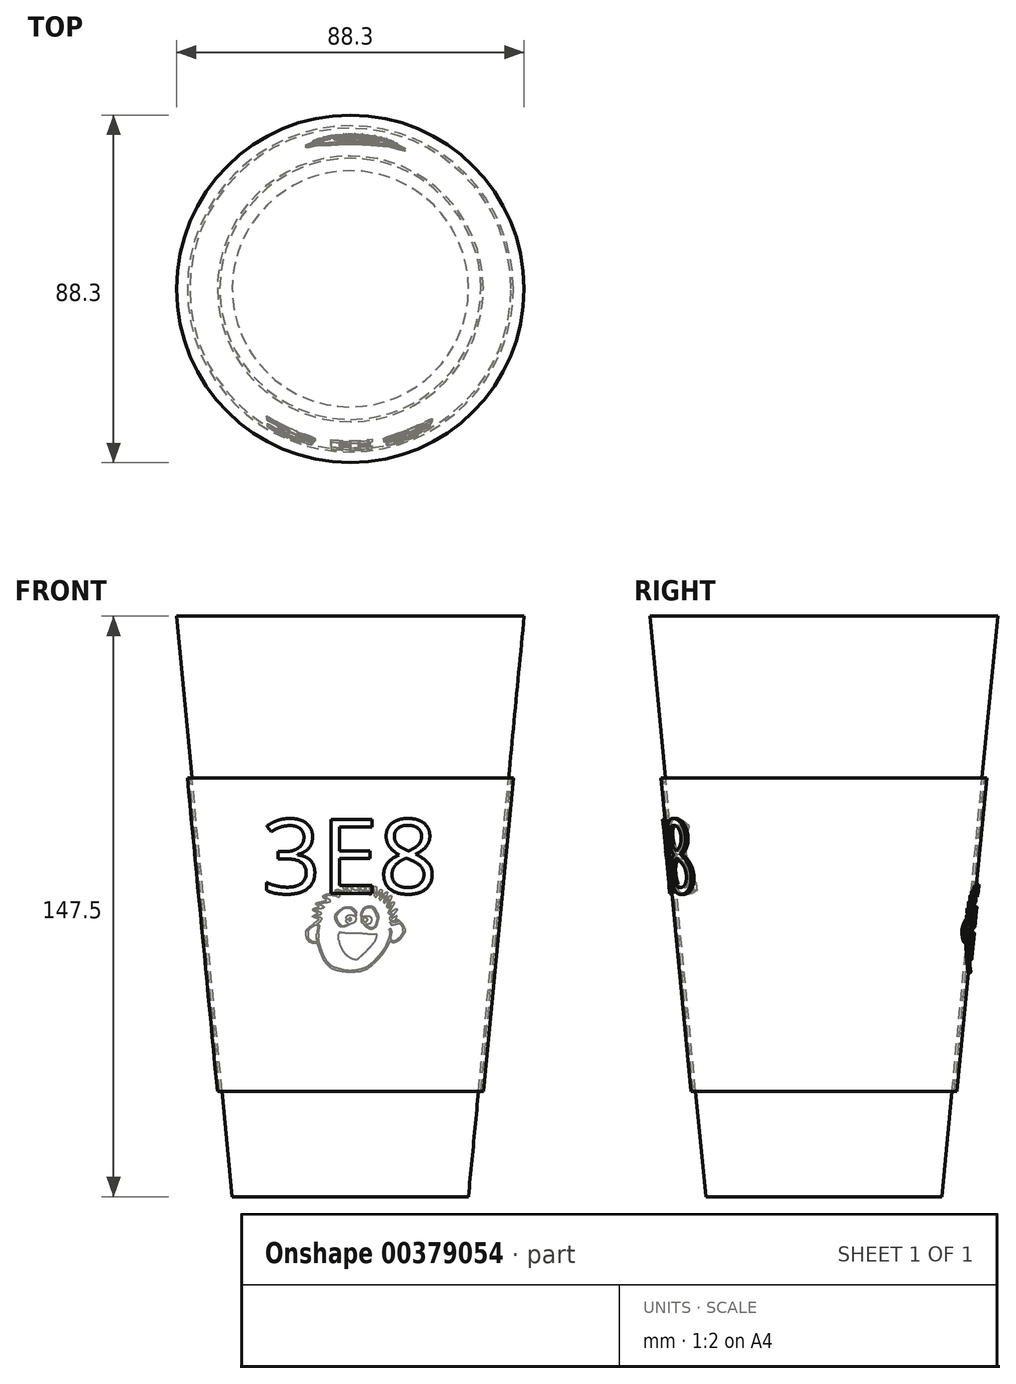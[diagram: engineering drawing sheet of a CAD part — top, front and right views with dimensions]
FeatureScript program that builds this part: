
annotation { "Feature Type Name" : "Feature", "Feature Type Description" : "" }
export const myFeature = defineFeature(function(context is Context, id is Id, definition is map)
    precondition{}
    {
        {
            var Q0;
            Q0=qCreatedBy(makeId("Top.planeOp"),FACE);
            var sketch = newSketch(context, id + "F0", { "sketchPlane" : qUnion([Q0])});
            skCircle(sketch, "E0", {"center": v(0, 0) * mm, "radius": 30 * mm});
            skSolve(sketch);
        }
        {
            var Q0;
            Q0=qCreatedBy(makeId("Top.planeOp"),FACE);
            cPlane(context, id + "F1", {"entities" : qUnion([Q0]), "cplaneType" : CPlaneType.OFFSET, "offset" : 147.5 * mm, "width" : 150 * mm, "height" : 150 * mm});
        }
        {
            var Q0;
            Q0=qCreatedBy(id+"F1.planeOp",FACE);
            var sketch = newSketch(context, id + "F2", { "sketchPlane" : qUnion([Q0])});
            skCircle(sketch, "E1", {"center": v(0, 0) * mm, "radius": 44.15 * mm});
            skSolve(sketch);
        }
        {
            var Q0;
            Q0=makeQuery(id+"F0.imprint","IMPRINT",FACE,{"disambiguationData":[TD([[makeQuery(id+"F0.imprint","IMPRINT",EDGE,{"derivedFrom":sQuery(id+"F0.wireOp",EDGE,"E0")}),1.0]])]});
            var Q1;
            Q1=makeQuery(id+"F2.imprint","IMPRINT",FACE,{"disambiguationData":[TD([[makeQuery(id+"F2.imprint","IMPRINT",EDGE,{"derivedFrom":sQuery(id+"F2.wireOp",EDGE,"E1")}),1.0]])]});
            loft(context, id + "F3", {"sheetProfilesArray" : [{ "sheetProfileEntities" : qUnion([Q0]) }, { "sheetProfileEntities" : qUnion([Q1]) }]});
        }
        {
            var Q0;
            Q0=qCreatedBy(makeId("Front.planeOp"),FACE);
            var sketch = newSketch(context, id + "F4", { "sketchPlane" : qUnion([Q0])});
            skLineSegment(sketch, "E2", {"start": v(44.15, 147.5) * mm, "end": v(30, 0) * mm, "construction": true});
            skLineSegment(sketch, "E3", {"start": v(-30, 0) * mm, "end": v(-44.15, 147.5) * mm, "construction": true});
            skLineSegment(sketch, "E4", {"start": v(0, 0) * mm, "end": v(0, 147.5) * mm, "construction": true});
            skLineSegment(sketch, "E5", {"start": v(-40.21, 106.44) * mm, "end": v(-40.81, 106.44) * mm, "construction": true});
            skLineSegment(sketch, "E6", {"start": v(-40.81, 106.44) * mm, "end": v(-33.18, 26.86) * mm});
            skLineSegment(sketch, "E7", {"start": v(-33.18, 26.86) * mm, "end": v(-33.77, 26.8) * mm});
            skLineSegment(sketch, "E8", {"start": v(-33.77, 26.8) * mm, "end": v(-41.41, 106.44) * mm});
            skLineSegment(sketch, "E9", {"start": v(-41.41, 106.44) * mm, "end": v(-40.81, 106.44) * mm});
            skLineSegment(sketch, "E10", {"start": v(-41.41, 106.44) * mm, "end": v(-42.01, 106.44) * mm, "construction": true});
            skLineSegment(sketch, "E11", {"start": v(-42.01, 106.44) * mm, "end": v(-62.01, 106.44) * mm});
            skLineSegment(sketch, "E12", {"start": v(-62.01, 106.44) * mm, "end": v(-54.37, 26.8) * mm});
            skLineSegment(sketch, "E13", {"start": v(-54.37, 26.8) * mm, "end": v(-34.55, 28.7) * mm});
            skLineSegment(sketch, "E14", {"start": v(-34.55, 28.7) * mm, "end": v(-42.01, 106.44) * mm});
            skSolve(sketch);
        }
        {
            var Q0;
            Q0=makeQuery(id+"F4.imprint","IMPRINT",FACE,{"disambiguationData":[TD([[makeQuery(id+"F4.imprint","IMPRINT",EDGE,{"derivedFrom":sQuery(id+"F4.wireOp",EDGE,"E6")}),-1.0]])]});
            var Q1;
            Q1=sQuery(id+"F4.wireOp",EDGE,"E4");
            revolve(context, id + "F5", {"entities" : qUnion([Q0]), "axis" : qUnion([Q1]), "revolveType" : RevolveType.FULL});
        }
        {
            var Q0;
            Q0=qCreatedBy(makeId("Front.planeOp"),FACE);
            cPlane(context, id + "F6", {"entities" : qUnion([Q0]), "cplaneType" : CPlaneType.OFFSET, "offset" : 45 * mm, "width" : 150 * mm, "height" : 150 * mm});
        }
        {
            var Q0;
            Q0=qCreatedBy(makeId("Front.planeOp"),FACE);
            cPlane(context, id + "F7", {"entities" : qUnion([Q0]), "cplaneType" : CPlaneType.OFFSET, "offset" : 50 * mm, "oppositeDirection" : true, "width" : 150 * mm, "height" : 150 * mm});
        }
        {
            var Q0;
            Q0=qCreatedBy(id+"F6.planeOp",FACE);
            var sketch = newSketch(context, id + "F8", { "sketchPlane" : qUnion([Q0])});
            skLineSegment(sketch, "E15.0", {"start": v(41.41, 106.44) * mm, "end": v(-41.41, 106.44) * mm, "construction": true});
            skLineSegment(sketch, "E16.0", {"start": v(33.77, 26.8) * mm, "end": v(-33.77, 26.8) * mm, "construction": true});
            skText(sketch, "E17", { "text": "3E8", "fontName": "OpenSans-Regular.ttf"});
            skLineSegment(sketch, "E18", {"start": v(0, 81.8) * mm, "end": v(0, 106.44) * mm, "construction": true});
            skLineSegment(sketch, "E19", {"start": v(0, 51.43) * mm, "end": v(0, 26.8) * mm, "construction": true});
            const initialGuessF8  = {"E17": [-0.0225, 0.07707, 1, 0, 0.01892]};
            skSetInitialGuess(sketch, initialGuessF8);
            skSolve(sketch);
        }
        {
            var Q0;
            Q0=qCreatedBy(id+"F7.planeOp",FACE);
            var sketch = newSketch(context, id + "F9", { "sketchPlane" : qUnion([Q0])});
            skPoint(sketch, "E20.0", {"position": v(0, 81.8) * mm});
            skLineSegment(sketch, "E21", {"start": v(-7.97, 70.42) * mm, "end": v(-9.11, 69.59) * mm});
            skLineSegment(sketch, "E22", {"start": v(-9.11, 69.59) * mm, "end": v(-9.2, 69.3) * mm});
            skLineSegment(sketch, "E23", {"start": v(-9.2, 69.3) * mm, "end": v(-10.22, 68.66) * mm});
            skLineSegment(sketch, "E24", {"start": v(-10.22, 68.66) * mm, "end": v(-10.84, 68.07) * mm});
            skLineSegment(sketch, "E25", {"start": v(-10.84, 68.07) * mm, "end": v(-11.27, 67.43) * mm});
            skLineSegment(sketch, "E26", {"start": v(-11.27, 67.43) * mm, "end": v(-11.27, 66.6) * mm});
            skLineSegment(sketch, "E27", {"start": v(-11.27, 66.6) * mm, "end": v(-10.97, 65.33) * mm});
            skLineSegment(sketch, "E28", {"start": v(-10.97, 65.33) * mm, "end": v(-10.29, 64.62) * mm});
            skLineSegment(sketch, "E29", {"start": v(-10.29, 64.62) * mm, "end": v(-9.45, 64.34) * mm});
            skLineSegment(sketch, "E30", {"start": v(-8.34, 64.34) * mm, "end": v(-7.57, 62) * mm});
            skLineSegment(sketch, "E31", {"start": v(-7.57, 62) * mm, "end": v(-6.64, 59.9) * mm});
            skLineSegment(sketch, "E32", {"start": v(-6.64, 59.9) * mm, "end": v(-5.4, 58.47) * mm});
            skLineSegment(sketch, "E33", {"start": v(-5.4, 58.47) * mm, "end": v(-4.48, 57.76) * mm});
            skLineSegment(sketch, "E34", {"start": v(-4.48, 57.76) * mm, "end": v(-3.1, 57.36) * mm});
            skLineSegment(sketch, "E35", {"start": v(-3.1, 57.36) * mm, "end": v(-1.77, 57.1) * mm});
            skLineSegment(sketch, "E36", {"start": v(-1.77, 57.1) * mm, "end": v(0.1, 56.93) * mm});
            skLineSegment(sketch, "E37", {"start": v(0.1, 56.93) * mm, "end": v(2.49, 57.16) * mm});
            skLineSegment(sketch, "E38", {"start": v(2.49, 57.16) * mm, "end": v(4.18, 57.73) * mm});
            skLineSegment(sketch, "E39", {"start": v(4.18, 57.73) * mm, "end": v(5.76, 58.97) * mm});
            skLineSegment(sketch, "E40", {"start": v(5.76, 58.97) * mm, "end": v(7.97, 61.32) * mm});
            skLineSegment(sketch, "E41", {"start": v(7.97, 61.32) * mm, "end": v(9.28, 63.32) * mm});
            skLineSegment(sketch, "E42", {"start": v(9.28, 63.32) * mm, "end": v(9.91, 64.6) * mm});
            skLineSegment(sketch, "E43", {"start": v(9.91, 64.6) * mm, "end": v(10.1, 65.03) * mm});
            skLineSegment(sketch, "E44", {"start": v(10.1, 65.03) * mm, "end": v(10.42, 64.65) * mm});
            skLineSegment(sketch, "E45", {"start": v(10.42, 64.65) * mm, "end": v(10.86, 64.46) * mm});
            skLineSegment(sketch, "E46", {"start": v(10.86, 64.46) * mm, "end": v(11.72, 64.69) * mm});
            skLineSegment(sketch, "E47", {"start": v(11.72, 64.69) * mm, "end": v(12.55, 65.28) * mm});
            skLineSegment(sketch, "E48", {"start": v(12.55, 65.28) * mm, "end": v(13.79, 67.03) * mm});
            skLineSegment(sketch, "E49", {"start": v(13.79, 67.03) * mm, "end": v(13.94, 67.9) * mm});
            skLineSegment(sketch, "E50", {"start": v(13.94, 67.9) * mm, "end": v(13.18, 69.37) * mm});
            skLineSegment(sketch, "E51", {"start": v(13.18, 69.37) * mm, "end": v(12.55, 69.95) * mm});
            skLineSegment(sketch, "E52", {"start": v(12.55, 69.95) * mm, "end": v(12.08, 70.37) * mm});
            skLineSegment(sketch, "E53", {"start": v(12.08, 70.37) * mm, "end": v(11.6, 70.56) * mm});
            skLineSegment(sketch, "E54", {"start": v(11.6, 70.56) * mm, "end": v(11.47, 70.56) * mm});
            skLineSegment(sketch, "E55", {"start": v(11.47, 70.56) * mm, "end": v(11.81, 71.34) * mm});
            skLineSegment(sketch, "E56", {"start": v(11.81, 71.34) * mm, "end": v(11.7, 71.38) * mm});
            skLineSegment(sketch, "E57", {"start": v(11.7, 71.38) * mm, "end": v(10.89, 70.96) * mm});
            skLineSegment(sketch, "E58", {"start": v(10.89, 70.96) * mm, "end": v(10.68, 70.77) * mm});
            skLineSegment(sketch, "E59", {"start": v(10.68, 70.77) * mm, "end": v(10.44, 70.77) * mm});
            skLineSegment(sketch, "E60", {"start": v(10.44, 70.77) * mm, "end": v(10.59, 71.2) * mm});
            skLineSegment(sketch, "E61", {"start": v(10.59, 71.2) * mm, "end": v(11.24, 71.99) * mm});
            skLineSegment(sketch, "E62", {"start": v(11.24, 71.99) * mm, "end": v(11.98, 73) * mm});
            skLineSegment(sketch, "E63", {"start": v(11.98, 73) * mm, "end": v(11.68, 73.2) * mm});
            skLineSegment(sketch, "E64", {"start": v(11.68, 73.2) * mm, "end": v(10.17, 72.27) * mm});
            skLineSegment(sketch, "E65", {"start": v(10.17, 72.27) * mm, "end": v(10.04, 72.32) * mm});
            skLineSegment(sketch, "E66", {"start": v(10.04, 72.32) * mm, "end": v(10.09, 72.64) * mm});
            skLineSegment(sketch, "E67", {"start": v(10.09, 72.64) * mm, "end": v(11.15, 74.49) * mm});
            skLineSegment(sketch, "E68", {"start": v(11.15, 74.49) * mm, "end": v(11.15, 74.8) * mm});
            skLineSegment(sketch, "E69", {"start": v(11.15, 74.8) * mm, "end": v(11, 74.9) * mm});
            skLineSegment(sketch, "E70", {"start": v(11, 74.9) * mm, "end": v(10.77, 74.85) * mm});
            skLineSegment(sketch, "E71", {"start": v(10.77, 74.85) * mm, "end": v(9.75, 73.9) * mm});
            skLineSegment(sketch, "E72", {"start": v(9.75, 73.9) * mm, "end": v(9.65, 73.9) * mm});
            skLineSegment(sketch, "E73", {"start": v(9.65, 73.9) * mm, "end": v(9.65, 74.05) * mm});
            skLineSegment(sketch, "E74", {"start": v(9.65, 74.05) * mm, "end": v(10.45, 76.07) * mm});
            skLineSegment(sketch, "E75", {"start": v(10.45, 76.07) * mm, "end": v(10.4, 76.41) * mm});
            skLineSegment(sketch, "E76", {"start": v(10.4, 76.41) * mm, "end": v(10.2, 76.54) * mm});
            skLineSegment(sketch, "E77", {"start": v(10.2, 76.54) * mm, "end": v(9.7, 76.15) * mm});
            skLineSegment(sketch, "E78", {"start": v(9.7, 76.15) * mm, "end": v(8.97, 75.29) * mm});
            skLineSegment(sketch, "E79", {"start": v(8.97, 75.29) * mm, "end": v(8.87, 75.29) * mm});
            skLineSegment(sketch, "E80", {"start": v(8.87, 75.29) * mm, "end": v(9.45, 77.3) * mm});
            skLineSegment(sketch, "E81", {"start": v(9.45, 77.3) * mm, "end": v(9.37, 77.45) * mm});
            skLineSegment(sketch, "E82", {"start": v(9.37, 77.45) * mm, "end": v(9.17, 77.45) * mm});
            skLineSegment(sketch, "E83", {"start": v(9.17, 77.45) * mm, "end": v(8.95, 77.28) * mm});
            skLineSegment(sketch, "E84", {"start": v(8.95, 77.28) * mm, "end": v(7.97, 76) * mm});
            skLineSegment(sketch, "E85", {"start": v(7.97, 76) * mm, "end": v(7.86, 76) * mm});
            skLineSegment(sketch, "E86", {"start": v(7.86, 76) * mm, "end": v(8.1, 77.73) * mm});
            skLineSegment(sketch, "E87", {"start": v(8.1, 77.73) * mm, "end": v(7.92, 78.06) * mm});
            skLineSegment(sketch, "E88", {"start": v(7.92, 78.06) * mm, "end": v(7.68, 78.06) * mm});
            skLineSegment(sketch, "E89", {"start": v(7.68, 78.06) * mm, "end": v(6.68, 76.77) * mm});
            skLineSegment(sketch, "E90", {"start": v(6.68, 76.77) * mm, "end": v(6.55, 76.77) * mm});
            skLineSegment(sketch, "E91", {"start": v(6.55, 76.77) * mm, "end": v(6.6, 77.7) * mm});
            skLineSegment(sketch, "E92", {"start": v(6.6, 77.7) * mm, "end": v(6.6, 78.68) * mm});
            skLineSegment(sketch, "E93", {"start": v(6.6, 78.68) * mm, "end": v(6.41, 78.84) * mm});
            skLineSegment(sketch, "E94", {"start": v(6.41, 78.84) * mm, "end": v(6.14, 78.84) * mm});
            skLineSegment(sketch, "E95", {"start": v(6.14, 78.84) * mm, "end": v(5.9, 78.6) * mm});
            skLineSegment(sketch, "E96", {"start": v(5.9, 78.6) * mm, "end": v(5.13, 77.16) * mm});
            skLineSegment(sketch, "E97", {"start": v(5.13, 77.16) * mm, "end": v(5.04, 77.22) * mm});
            skLineSegment(sketch, "E98", {"start": v(5.04, 77.22) * mm, "end": v(4.7, 78.9) * mm});
            skLineSegment(sketch, "E99", {"start": v(4.7, 78.9) * mm, "end": v(4.48, 79) * mm});
            skLineSegment(sketch, "E100", {"start": v(4.48, 79) * mm, "end": v(4.22, 78.8) * mm});
            skLineSegment(sketch, "E101", {"start": v(4.22, 78.8) * mm, "end": v(3.89, 77.57) * mm});
            skLineSegment(sketch, "E102", {"start": v(3.89, 77.57) * mm, "end": v(3.45, 78.7) * mm});
            skLineSegment(sketch, "E103", {"start": v(3.45, 78.7) * mm, "end": v(3.22, 78.87) * mm});
            skLineSegment(sketch, "E104", {"start": v(3.22, 78.87) * mm, "end": v(3, 78.87) * mm});
            skLineSegment(sketch, "E105", {"start": v(3, 78.87) * mm, "end": v(2.8, 78.8) * mm});
            skLineSegment(sketch, "E106", {"start": v(2.8, 78.8) * mm, "end": v(2.6, 77.83) * mm});
            skLineSegment(sketch, "E107", {"start": v(2.6, 77.83) * mm, "end": v(1.49, 79.03) * mm});
            skLineSegment(sketch, "E108", {"start": v(1.49, 79.03) * mm, "end": v(1.02, 79.03) * mm});
            skLineSegment(sketch, "E109", {"start": v(1.02, 79.03) * mm, "end": v(0.87, 78.84) * mm});
            skLineSegment(sketch, "E110", {"start": v(0.87, 78.84) * mm, "end": v(0.87, 78.75) * mm});
            skLineSegment(sketch, "E111", {"start": v(0.87, 78.75) * mm, "end": v(-0.32, 79.35) * mm});
            skLineSegment(sketch, "E112", {"start": v(-0.32, 79.35) * mm, "end": v(-0.61, 79.25) * mm});
            skLineSegment(sketch, "E113", {"start": v(-0.61, 79.25) * mm, "end": v(-0.61, 79.04) * mm});
            skLineSegment(sketch, "E114", {"start": v(-0.61, 79.04) * mm, "end": v(-0.47, 78.58) * mm});
            skLineSegment(sketch, "E115", {"start": v(-0.47, 78.58) * mm, "end": v(-1.6, 78.92) * mm});
            skLineSegment(sketch, "E116", {"start": v(-1.6, 78.92) * mm, "end": v(-1.79, 78.81) * mm});
            skLineSegment(sketch, "E117", {"start": v(-1.79, 78.81) * mm, "end": v(-1.79, 78.5) * mm});
            skLineSegment(sketch, "E118", {"start": v(-1.79, 78.5) * mm, "end": v(-1.43, 77.51) * mm});
            skLineSegment(sketch, "E119", {"start": v(-1.43, 77.51) * mm, "end": v(-2.23, 77.79) * mm});
            skLineSegment(sketch, "E120", {"start": v(-2.23, 77.79) * mm, "end": v(-3.1, 78.08) * mm});
            skLineSegment(sketch, "E121", {"start": v(-3.1, 78.08) * mm, "end": v(-3.66, 77.99) * mm});
            skLineSegment(sketch, "E122", {"start": v(-3.66, 77.99) * mm, "end": v(-3.83, 77.68) * mm});
            skLineSegment(sketch, "E123", {"start": v(-3.83, 77.68) * mm, "end": v(-3.4, 76.78) * mm});
            skLineSegment(sketch, "E124", {"start": v(-3.4, 76.78) * mm, "end": v(-4.02, 77.02) * mm});
            skLineSegment(sketch, "E125", {"start": v(-4.02, 77.02) * mm, "end": v(-5.14, 77.02) * mm});
            skLineSegment(sketch, "E126", {"start": v(-5.14, 77.02) * mm, "end": v(-6.18, 76.84) * mm});
            skLineSegment(sketch, "E127", {"start": v(-6.18, 76.84) * mm, "end": v(-6.75, 76.59) * mm});
            skLineSegment(sketch, "E128", {"start": v(-6.75, 76.59) * mm, "end": v(-6.96, 76.3) * mm});
            skLineSegment(sketch, "E129", {"start": v(-6.96, 76.3) * mm, "end": v(-6.8, 75.94) * mm});
            skLineSegment(sketch, "E130", {"start": v(-6.8, 75.94) * mm, "end": v(-6.15, 75.4) * mm});
            skLineSegment(sketch, "E131", {"start": v(-6.15, 75.4) * mm, "end": v(-6.02, 75.25) * mm});
            skLineSegment(sketch, "E132", {"start": v(-6.02, 75.25) * mm, "end": v(-6.6, 75.16) * mm});
            skLineSegment(sketch, "E133", {"start": v(-6.6, 75.16) * mm, "end": v(-8.56, 74.66) * mm});
            skLineSegment(sketch, "E134", {"start": v(-8.56, 74.66) * mm, "end": v(-8.78, 74.45) * mm});
            skLineSegment(sketch, "E135", {"start": v(-8.78, 74.45) * mm, "end": v(-8.78, 74.26) * mm});
            skLineSegment(sketch, "E136", {"start": v(-8.78, 74.26) * mm, "end": v(-7.98, 73.75) * mm});
            skLineSegment(sketch, "E137", {"start": v(-7.98, 73.75) * mm, "end": v(-7.98, 73.63) * mm});
            skLineSegment(sketch, "E138", {"start": v(-7.98, 73.63) * mm, "end": v(-9.09, 73.31) * mm});
            skLineSegment(sketch, "E139", {"start": v(-9.09, 73.31) * mm, "end": v(-9.47, 73.05) * mm});
            skLineSegment(sketch, "E140", {"start": v(-9.47, 73.05) * mm, "end": v(-9.47, 72.82) * mm});
            skLineSegment(sketch, "E141", {"start": v(-9.47, 72.82) * mm, "end": v(-9.22, 72.53) * mm});
            skLineSegment(sketch, "E142", {"start": v(-9.22, 72.53) * mm, "end": v(-8.26, 72.03) * mm});
            skLineSegment(sketch, "E143", {"start": v(-8.26, 72.03) * mm, "end": v(-8.22, 71.93) * mm});
            skLineSegment(sketch, "E144", {"start": v(-8.22, 71.93) * mm, "end": v(-8.85, 71.7) * mm});
            skLineSegment(sketch, "E145", {"start": v(-8.85, 71.7) * mm, "end": v(-9.5, 71.28) * mm});
            skLineSegment(sketch, "E146", {"start": v(-9.5, 71.28) * mm, "end": v(-9.59, 71.1) * mm});
            skLineSegment(sketch, "E147", {"start": v(-9.59, 71.1) * mm, "end": v(-9.21, 70.92) * mm});
            skLineSegment(sketch, "E148", {"start": v(-9.21, 70.92) * mm, "end": v(-8.4, 70.65) * mm});
            skLineSegment(sketch, "E149", {"start": v(-8.4, 70.65) * mm, "end": v(-8.02, 70.57) * mm});
            skLineSegment(sketch, "E150", {"start": v(-8.02, 70.57) * mm, "end": v(-7.9, 70.54) * mm});
            skLineSegment(sketch, "E151", {"start": v(-7.9, 70.54) * mm, "end": v(-7.97, 70.42) * mm});
            skLineSegment(sketch, "E152", {"start": v(-8.88, 69.08) * mm, "end": v(-10.06, 68.35) * mm});
            skLineSegment(sketch, "E153", {"start": v(-10.06, 68.35) * mm, "end": v(-10.74, 67.43) * mm});
            skLineSegment(sketch, "E154", {"start": v(-10.74, 67.43) * mm, "end": v(-10.74, 65.98) * mm});
            skLineSegment(sketch, "E155", {"start": v(-10.74, 65.98) * mm, "end": v(-10.28, 65.21) * mm});
            skLineSegment(sketch, "E156", {"start": v(-10.28, 65.21) * mm, "end": v(-9.42, 64.67) * mm});
            skLineSegment(sketch, "E157", {"start": v(-9.42, 64.67) * mm, "end": v(-8.38, 64.67) * mm});
            skLineSegment(sketch, "E158", {"start": v(-8.38, 64.67) * mm, "end": v(-8.54, 65.33) * mm});
            skLineSegment(sketch, "E159", {"start": v(-8.54, 65.33) * mm, "end": v(-8.54, 66.79) * mm});
            skLineSegment(sketch, "E160", {"start": v(-8.54, 66.79) * mm, "end": v(-8.36, 67.99) * mm});
            skLineSegment(sketch, "E161", {"start": v(-8.36, 67.99) * mm, "end": v(-8.2, 68.68) * mm});
            skLineSegment(sketch, "E162", {"start": v(-8.2, 68.68) * mm, "end": v(-8.43, 68.95) * mm});
            skLineSegment(sketch, "E163", {"start": v(-8.43, 68.95) * mm, "end": v(-8.88, 69.08) * mm});
            skLineSegment(sketch, "E164", {"start": v(-2.83, 67.14) * mm, "end": v(-1.3, 66.94) * mm});
            skLineSegment(sketch, "E165", {"start": v(-1.3, 66.94) * mm, "end": v(0.26, 66.88) * mm});
            skLineSegment(sketch, "E166", {"start": v(0.26, 66.88) * mm, "end": v(2.2, 66.93) * mm});
            skLineSegment(sketch, "E167", {"start": v(2.2, 66.93) * mm, "end": v(4.76, 66.64) * mm});
            skLineSegment(sketch, "E168", {"start": v(4.76, 66.64) * mm, "end": v(6.7, 66.59) * mm});
            skLineSegment(sketch, "E169", {"start": v(6.7, 66.59) * mm, "end": v(6.78, 66.45) * mm});
            skLineSegment(sketch, "E170", {"start": v(6.78, 66.45) * mm, "end": v(6.68, 65.93) * mm});
            skLineSegment(sketch, "E171", {"start": v(6.68, 65.93) * mm, "end": v(6.27, 64.87) * mm});
            skLineSegment(sketch, "E172", {"start": v(6.27, 64.87) * mm, "end": v(5.29, 63.7) * mm});
            skLineSegment(sketch, "E173", {"start": v(5.29, 63.7) * mm, "end": v(4.57, 62.93) * mm});
            skLineSegment(sketch, "E174", {"start": v(4.57, 62.93) * mm, "end": v(4.01, 62.31) * mm});
            skLineSegment(sketch, "E175", {"start": v(4.01, 62.31) * mm, "end": v(3.54, 61.87) * mm});
            skLineSegment(sketch, "E176", {"start": v(3.54, 61.87) * mm, "end": v(2.85, 61.26) * mm});
            skLineSegment(sketch, "E177", {"start": v(2.85, 61.26) * mm, "end": v(2.22, 60.67) * mm});
            skLineSegment(sketch, "E178", {"start": v(2.22, 60.67) * mm, "end": v(1.68, 60.27) * mm});
            skLineSegment(sketch, "E179", {"start": v(1.68, 60.27) * mm, "end": v(1.46, 60.23) * mm});
            skLineSegment(sketch, "E180", {"start": v(1.46, 60.23) * mm, "end": v(1.03, 60.34) * mm});
            skLineSegment(sketch, "E181", {"start": v(1.03, 60.34) * mm, "end": v(0.5, 60.5) * mm});
            skLineSegment(sketch, "E182", {"start": v(0.5, 60.5) * mm, "end": v(0.14, 60.64) * mm});
            skLineSegment(sketch, "E183", {"start": v(0.14, 60.64) * mm, "end": v(-0.31, 60.92) * mm});
            skLineSegment(sketch, "E184", {"start": v(-0.31, 60.92) * mm, "end": v(-0.92, 61.32) * mm});
            skLineSegment(sketch, "E185", {"start": v(-0.92, 61.32) * mm, "end": v(-1.55, 61.94) * mm});
            skLineSegment(sketch, "E186", {"start": v(-1.55, 61.94) * mm, "end": v(-2.13, 62.79) * mm});
            skLineSegment(sketch, "E187", {"start": v(-2.13, 62.79) * mm, "end": v(-2.67, 63.97) * mm});
            skLineSegment(sketch, "E188", {"start": v(-2.67, 63.97) * mm, "end": v(-2.97, 65.25) * mm});
            skLineSegment(sketch, "E189", {"start": v(-2.97, 65.25) * mm, "end": v(-2.97, 66.63) * mm});
            skLineSegment(sketch, "E190", {"start": v(-2.97, 66.63) * mm, "end": v(-2.83, 67.14) * mm});
            skLineSegment(sketch, "E191", {"start": v(-8.34, 69.38) * mm, "end": v(-7.92, 68.9) * mm});
            skLineSegment(sketch, "E192", {"start": v(-7.92, 68.9) * mm, "end": v(-7.74, 68.73) * mm});
            skLineSegment(sketch, "E193", {"start": v(-7.74, 68.73) * mm, "end": v(-7.84, 68.39) * mm});
            skLineSegment(sketch, "E194", {"start": v(-7.84, 68.39) * mm, "end": v(-7.97, 67.53) * mm});
            skLineSegment(sketch, "E195", {"start": v(-7.97, 67.53) * mm, "end": v(-8.08, 66.83) * mm});
            skLineSegment(sketch, "E196", {"start": v(-8.08, 66.83) * mm, "end": v(-8.08, 65.8) * mm});
            skLineSegment(sketch, "E197", {"start": v(-8.08, 65.8) * mm, "end": v(-7.88, 64.6) * mm});
            skLineSegment(sketch, "E198", {"start": v(-7.88, 64.6) * mm, "end": v(-7.44, 63.1) * mm});
            skLineSegment(sketch, "E199", {"start": v(-7.44, 63.1) * mm, "end": v(-6.88, 61.52) * mm});
            skLineSegment(sketch, "E200", {"start": v(-6.88, 61.52) * mm, "end": v(-6.05, 59.93) * mm});
            skLineSegment(sketch, "E201", {"start": v(-6.05, 59.93) * mm, "end": v(-5.11, 58.89) * mm});
            skLineSegment(sketch, "E202", {"start": v(-5.11, 58.89) * mm, "end": v(-4.3, 58.31) * mm});
            skLineSegment(sketch, "E203", {"start": v(-4.3, 58.31) * mm, "end": v(-2.63, 57.84) * mm});
            skLineSegment(sketch, "E204", {"start": v(-2.63, 57.84) * mm, "end": v(-1.16, 57.46) * mm});
            skLineSegment(sketch, "E205", {"start": v(-1.16, 57.46) * mm, "end": v(-0.05, 57.4) * mm});
            skLineSegment(sketch, "E206", {"start": v(-0.05, 57.4) * mm, "end": v(0.78, 57.46) * mm});
            skLineSegment(sketch, "E207", {"start": v(0.78, 57.46) * mm, "end": v(1.86, 57.58) * mm});
            skLineSegment(sketch, "E208", {"start": v(1.86, 57.58) * mm, "end": v(2.93, 57.87) * mm});
            skLineSegment(sketch, "E209", {"start": v(2.93, 57.87) * mm, "end": v(4, 58.23) * mm});
            skLineSegment(sketch, "E210", {"start": v(4, 58.23) * mm, "end": v(5.48, 59.35) * mm});
            skLineSegment(sketch, "E211", {"start": v(5.48, 59.35) * mm, "end": v(7.09, 61.04) * mm});
            skLineSegment(sketch, "E212", {"start": v(7.09, 61.04) * mm, "end": v(7.97, 62.16) * mm});
            skLineSegment(sketch, "E213", {"start": v(7.97, 62.16) * mm, "end": v(8.86, 63.44) * mm});
            skLineSegment(sketch, "E214", {"start": v(8.86, 63.44) * mm, "end": v(9.4, 64.87) * mm});
            skLineSegment(sketch, "E215", {"start": v(9.4, 64.87) * mm, "end": v(9.83, 65.9) * mm});
            skLineSegment(sketch, "E216", {"start": v(9.83, 65.9) * mm, "end": v(10.08, 67.1) * mm});
            skLineSegment(sketch, "E217", {"start": v(10.08, 67.1) * mm, "end": v(10.08, 67.74) * mm});
            skLineSegment(sketch, "E218", {"start": v(10.08, 67.74) * mm, "end": v(9.97, 67.74) * mm});
            skLineSegment(sketch, "E219", {"start": v(9.97, 67.74) * mm, "end": v(9.84, 67.76) * mm});
            skLineSegment(sketch, "E220", {"start": v(9.84, 67.76) * mm, "end": v(9.84, 67.88) * mm});
            skLineSegment(sketch, "E221", {"start": v(9.84, 67.88) * mm, "end": v(10.03, 68.06) * mm});
            skLineSegment(sketch, "E222", {"start": v(10.03, 68.06) * mm, "end": v(10.17, 68.08) * mm});
            skLineSegment(sketch, "E223", {"start": v(10.17, 68.08) * mm, "end": v(10.34, 67.96) * mm});
            skLineSegment(sketch, "E224", {"start": v(10.34, 67.96) * mm, "end": v(10.5, 67.69) * mm});
            skLineSegment(sketch, "E225", {"start": v(10.5, 67.69) * mm, "end": v(10.58, 67.23) * mm});
            skLineSegment(sketch, "E226", {"start": v(10.58, 67.23) * mm, "end": v(10.49, 66.6) * mm});
            skLineSegment(sketch, "E227", {"start": v(10.49, 66.6) * mm, "end": v(10.34, 65.97) * mm});
            skLineSegment(sketch, "E228", {"start": v(10.34, 65.97) * mm, "end": v(10.26, 65.55) * mm});
            skLineSegment(sketch, "E229", {"start": v(10.26, 65.55) * mm, "end": v(10.39, 65.17) * mm});
            skLineSegment(sketch, "E230", {"start": v(10.39, 65.17) * mm, "end": v(10.7, 64.99) * mm});
            skLineSegment(sketch, "E231", {"start": v(10.7, 64.99) * mm, "end": v(11.05, 64.86) * mm});
            skLineSegment(sketch, "E232", {"start": v(11.05, 64.86) * mm, "end": v(11.75, 65.17) * mm});
            skLineSegment(sketch, "E233", {"start": v(11.75, 65.17) * mm, "end": v(12.56, 65.93) * mm});
            skLineSegment(sketch, "E234", {"start": v(12.56, 65.93) * mm, "end": v(13.25, 67) * mm});
            skLineSegment(sketch, "E235", {"start": v(13.25, 67) * mm, "end": v(13.4, 67.5) * mm});
            skLineSegment(sketch, "E236", {"start": v(13.4, 67.5) * mm, "end": v(13.4, 68.15) * mm});
            skLineSegment(sketch, "E237", {"start": v(13.4, 68.15) * mm, "end": v(12.78, 69.24) * mm});
            skLineSegment(sketch, "E238", {"start": v(12.78, 69.24) * mm, "end": v(12.52, 69.48) * mm});
            skLineSegment(sketch, "E239", {"start": v(12.52, 69.48) * mm, "end": v(11.9, 69.33) * mm});
            skLineSegment(sketch, "E240", {"start": v(11.9, 69.33) * mm, "end": v(11.09, 69.13) * mm});
            skLineSegment(sketch, "E241", {"start": v(11.09, 69.13) * mm, "end": v(10.43, 69) * mm});
            skLineSegment(sketch, "E242", {"start": v(10.43, 69) * mm, "end": v(10.28, 69) * mm});
            skLineSegment(sketch, "E243", {"start": v(10.28, 69) * mm, "end": v(10.27, 69.2) * mm});
            skLineSegment(sketch, "E244", {"start": v(10.27, 69.2) * mm, "end": v(10.44, 69.36) * mm});
            skLineSegment(sketch, "E245", {"start": v(10.44, 69.36) * mm, "end": v(10.3, 69.52) * mm});
            skLineSegment(sketch, "E246", {"start": v(10.3, 69.52) * mm, "end": v(10.12, 69.6) * mm});
            skLineSegment(sketch, "E247", {"start": v(10.12, 69.6) * mm, "end": v(10.12, 69.77) * mm});
            skLineSegment(sketch, "E248", {"start": v(10.12, 69.77) * mm, "end": v(10.3, 70.1) * mm});
            skLineSegment(sketch, "E249", {"start": v(10.3, 70.1) * mm, "end": v(10.59, 70.36) * mm});
            skLineSegment(sketch, "E250", {"start": v(10.59, 70.36) * mm, "end": v(10.1, 70.36) * mm});
            skLineSegment(sketch, "E251", {"start": v(10.1, 70.36) * mm, "end": v(9.94, 70.53) * mm});
            skLineSegment(sketch, "E252", {"start": v(9.94, 70.53) * mm, "end": v(10.03, 70.96) * mm});
            skLineSegment(sketch, "E253", {"start": v(10.03, 70.96) * mm, "end": v(10.42, 71.57) * mm});
            skLineSegment(sketch, "E254", {"start": v(10.42, 71.57) * mm, "end": v(10.56, 71.86) * mm});
            skLineSegment(sketch, "E255", {"start": v(10.56, 71.86) * mm, "end": v(10.48, 72) * mm});
            skLineSegment(sketch, "E256", {"start": v(10.48, 72) * mm, "end": v(9.88, 71.85) * mm});
            skLineSegment(sketch, "E257", {"start": v(9.88, 71.85) * mm, "end": v(9.66, 72) * mm});
            skLineSegment(sketch, "E258", {"start": v(9.66, 72) * mm, "end": v(9.66, 72.35) * mm});
            skLineSegment(sketch, "E259", {"start": v(9.66, 72.35) * mm, "end": v(9.93, 73.09) * mm});
            skLineSegment(sketch, "E260", {"start": v(9.93, 73.09) * mm, "end": v(10.47, 74.03) * mm});
            skLineSegment(sketch, "E261", {"start": v(10.47, 74.03) * mm, "end": v(9.58, 73.5) * mm});
            skLineSegment(sketch, "E262", {"start": v(9.58, 73.5) * mm, "end": v(9.32, 73.5) * mm});
            skLineSegment(sketch, "E263", {"start": v(9.32, 73.5) * mm, "end": v(9.18, 73.79) * mm});
            skLineSegment(sketch, "E264", {"start": v(9.18, 73.79) * mm, "end": v(9.84, 75.7) * mm});
            skLineSegment(sketch, "E265", {"start": v(9.84, 75.7) * mm, "end": v(8.71, 74.66) * mm});
            skLineSegment(sketch, "E266", {"start": v(8.71, 74.66) * mm, "end": v(8.54, 74.64) * mm});
            skLineSegment(sketch, "E267", {"start": v(8.54, 74.64) * mm, "end": v(8.4, 74.84) * mm});
            skLineSegment(sketch, "E268", {"start": v(8.4, 74.84) * mm, "end": v(8.8, 76.51) * mm});
            skLineSegment(sketch, "E269", {"start": v(8.8, 76.51) * mm, "end": v(7.59, 75.33) * mm});
            skLineSegment(sketch, "E270", {"start": v(7.59, 75.33) * mm, "end": v(7.42, 75.44) * mm});
            skLineSegment(sketch, "E271", {"start": v(7.42, 75.44) * mm, "end": v(7.31, 75.7) * mm});
            skLineSegment(sketch, "E272", {"start": v(7.31, 75.7) * mm, "end": v(7.69, 77.47) * mm});
            skLineSegment(sketch, "E273", {"start": v(7.69, 77.47) * mm, "end": v(6.55, 76.14) * mm});
            skLineSegment(sketch, "E274", {"start": v(6.55, 76.14) * mm, "end": v(6.3, 76.14) * mm});
            skLineSegment(sketch, "E275", {"start": v(6.3, 76.14) * mm, "end": v(6.14, 76.35) * mm});
            skLineSegment(sketch, "E276", {"start": v(6.14, 76.35) * mm, "end": v(6.14, 78.32) * mm});
            skLineSegment(sketch, "E277", {"start": v(6.14, 78.32) * mm, "end": v(5.33, 76.88) * mm});
            skLineSegment(sketch, "E278", {"start": v(5.33, 76.88) * mm, "end": v(5.01, 76.69) * mm});
            skLineSegment(sketch, "E279", {"start": v(5.01, 76.69) * mm, "end": v(4.82, 76.77) * mm});
            skLineSegment(sketch, "E280", {"start": v(4.82, 76.77) * mm, "end": v(4.47, 77.98) * mm});
            skLineSegment(sketch, "E281", {"start": v(4.47, 77.98) * mm, "end": v(4.25, 77.26) * mm});
            skLineSegment(sketch, "E282", {"start": v(4.25, 77.26) * mm, "end": v(3.9, 76.91) * mm});
            skLineSegment(sketch, "E283", {"start": v(3.9, 76.91) * mm, "end": v(3.6, 77.02) * mm});
            skLineSegment(sketch, "E284", {"start": v(3.6, 77.02) * mm, "end": v(3.18, 78.02) * mm});
            skLineSegment(sketch, "E285", {"start": v(3.18, 78.02) * mm, "end": v(3.06, 77.5) * mm});
            skLineSegment(sketch, "E286", {"start": v(3.06, 77.5) * mm, "end": v(2.8, 77.27) * mm});
            skLineSegment(sketch, "E287", {"start": v(2.8, 77.27) * mm, "end": v(2.6, 77.27) * mm});
            skLineSegment(sketch, "E288", {"start": v(2.6, 77.27) * mm, "end": v(1.68, 78.09) * mm});
            skLineSegment(sketch, "E289", {"start": v(1.68, 78.09) * mm, "end": v(1.5, 77.88) * mm});
            skLineSegment(sketch, "E290", {"start": v(1.5, 77.88) * mm, "end": v(1.03, 77.88) * mm});
            skLineSegment(sketch, "E291", {"start": v(1.03, 77.88) * mm, "end": v(0.27, 78.6) * mm});
            skLineSegment(sketch, "E292", {"start": v(0.27, 78.6) * mm, "end": v(0.19, 78.51) * mm});
            skLineSegment(sketch, "E293", {"start": v(0.19, 78.51) * mm, "end": v(0.48, 78.02) * mm});
            skLineSegment(sketch, "E294", {"start": v(0.48, 78.02) * mm, "end": v(0.33, 77.84) * mm});
            skLineSegment(sketch, "E295", {"start": v(0.33, 77.84) * mm, "end": v(-0.36, 77.84) * mm});
            skLineSegment(sketch, "E296", {"start": v(-0.36, 77.84) * mm, "end": v(-1.11, 78.34) * mm});
            skLineSegment(sketch, "E297", {"start": v(-1.11, 78.34) * mm, "end": v(-1.17, 78.26) * mm});
            skLineSegment(sketch, "E298", {"start": v(-1.17, 78.26) * mm, "end": v(-0.93, 77.78) * mm});
            skLineSegment(sketch, "E299", {"start": v(-0.93, 77.78) * mm, "end": v(-0.93, 77.1) * mm});
            skLineSegment(sketch, "E300", {"start": v(-0.93, 77.1) * mm, "end": v(-1.17, 76.93) * mm});
            skLineSegment(sketch, "E301", {"start": v(-1.17, 76.93) * mm, "end": v(-3.31, 77.67) * mm});
            skLineSegment(sketch, "E302", {"start": v(-3.31, 77.67) * mm, "end": v(-2.56, 76.47) * mm});
            skLineSegment(sketch, "E303", {"start": v(-2.56, 76.47) * mm, "end": v(-2.79, 76.2) * mm});
            skLineSegment(sketch, "E304", {"start": v(-2.79, 76.2) * mm, "end": v(-3.16, 76.2) * mm});
            skLineSegment(sketch, "E305", {"start": v(-3.16, 76.2) * mm, "end": v(-3.58, 76.42) * mm});
            skLineSegment(sketch, "E306", {"start": v(-3.58, 76.42) * mm, "end": v(-4.57, 76.6) * mm});
            skLineSegment(sketch, "E307", {"start": v(-4.57, 76.6) * mm, "end": v(-5.7, 76.6) * mm});
            skLineSegment(sketch, "E308", {"start": v(-5.7, 76.6) * mm, "end": v(-6.49, 76.36) * mm});
            skLineSegment(sketch, "E309", {"start": v(-6.49, 76.36) * mm, "end": v(-6.39, 76.16) * mm});
            skLineSegment(sketch, "E310", {"start": v(-6.39, 76.16) * mm, "end": v(-5.08, 75.26) * mm});
            skLineSegment(sketch, "E311", {"start": v(-5.08, 75.26) * mm, "end": v(-5.03, 75.05) * mm});
            skLineSegment(sketch, "E312", {"start": v(-5.03, 75.05) * mm, "end": v(-5.4, 74.84) * mm});
            skLineSegment(sketch, "E313", {"start": v(-5.4, 74.84) * mm, "end": v(-6.58, 74.76) * mm});
            skLineSegment(sketch, "E314", {"start": v(-6.58, 74.76) * mm, "end": v(-7.87, 74.42) * mm});
            skLineSegment(sketch, "E315", {"start": v(-7.87, 74.42) * mm, "end": v(-8.04, 74.42) * mm});
            skLineSegment(sketch, "E316", {"start": v(-8.04, 74.42) * mm, "end": v(-8.04, 74.3) * mm});
            skLineSegment(sketch, "E317", {"start": v(-8.04, 74.3) * mm, "end": v(-6.75, 73.66) * mm});
            skLineSegment(sketch, "E318", {"start": v(-6.75, 73.66) * mm, "end": v(-6.75, 73.46) * mm});
            skLineSegment(sketch, "E319", {"start": v(-6.75, 73.46) * mm, "end": v(-6.84, 73.38) * mm});
            skLineSegment(sketch, "E320", {"start": v(-6.84, 73.38) * mm, "end": v(-8.84, 73.05) * mm});
            skLineSegment(sketch, "E321", {"start": v(-8.84, 73.05) * mm, "end": v(-8.81, 72.87) * mm});
            skLineSegment(sketch, "E322", {"start": v(-8.81, 72.87) * mm, "end": v(-7.57, 72.19) * mm});
            skLineSegment(sketch, "E323", {"start": v(-7.57, 72.19) * mm, "end": v(-7.35, 72.05) * mm});
            skLineSegment(sketch, "E324", {"start": v(-7.35, 72.05) * mm, "end": v(-7.31, 71.85) * mm});
            skLineSegment(sketch, "E325", {"start": v(-7.31, 71.85) * mm, "end": v(-8.86, 71.28) * mm});
            skLineSegment(sketch, "E326", {"start": v(-8.86, 71.28) * mm, "end": v(-7.37, 70.84) * mm});
            skLineSegment(sketch, "E327", {"start": v(-7.37, 70.84) * mm, "end": v(-7.37, 70.38) * mm});
            skLineSegment(sketch, "E328", {"start": v(-7.37, 70.38) * mm, "end": v(-7.49, 70.03) * mm});
            skLineSegment(sketch, "E329", {"start": v(-7.49, 70.03) * mm, "end": v(-8.34, 69.38) * mm});
            skLineSegment(sketch, "E330", {"start": v(-1.7, 73.48) * mm, "end": v(-2.67, 72.83) * mm});
            skLineSegment(sketch, "E331", {"start": v(-2.67, 72.83) * mm, "end": v(-3.73, 71.86) * mm});
            skLineSegment(sketch, "E332", {"start": v(-3.73, 71.86) * mm, "end": v(-3.95, 70.95) * mm});
            skLineSegment(sketch, "E333", {"start": v(-3.95, 70.95) * mm, "end": v(-3.82, 70.4) * mm});
            skLineSegment(sketch, "E334", {"start": v(-3.82, 70.4) * mm, "end": v(-3.4, 69.54) * mm});
            skLineSegment(sketch, "E335", {"start": v(-3.4, 69.54) * mm, "end": v(-2.97, 68.97) * mm});
            skLineSegment(sketch, "E336", {"start": v(-2.97, 68.97) * mm, "end": v(-2.49, 68.47) * mm});
            skLineSegment(sketch, "E337", {"start": v(-2.49, 68.47) * mm, "end": v(-1.11, 68.64) * mm});
            skLineSegment(sketch, "E338", {"start": v(-1.11, 68.64) * mm, "end": v(0.25, 69.35) * mm});
            skLineSegment(sketch, "E339", {"start": v(0.25, 69.35) * mm, "end": v(0.9, 69.53) * mm});
            skLineSegment(sketch, "E340", {"start": v(0.9, 69.53) * mm, "end": v(1.33, 70.04) * mm});
            skLineSegment(sketch, "E341", {"start": v(1.33, 70.04) * mm, "end": v(1.41, 70.56) * mm});
            skLineSegment(sketch, "E342", {"start": v(1.41, 70.56) * mm, "end": v(1.36, 71.05) * mm});
            skLineSegment(sketch, "E343", {"start": v(1.36, 71.05) * mm, "end": v(1.52, 72.28) * mm});
            skLineSegment(sketch, "E344", {"start": v(1.52, 72.28) * mm, "end": v(1.36, 72.59) * mm});
            skLineSegment(sketch, "E345", {"start": v(1.36, 72.59) * mm, "end": v(0.75, 73.24) * mm});
            skLineSegment(sketch, "E346", {"start": v(0.75, 73.24) * mm, "end": v(0.28, 73.56) * mm});
            skLineSegment(sketch, "E347", {"start": v(0.28, 73.56) * mm, "end": v(-0.3, 73.67) * mm});
            skLineSegment(sketch, "E348", {"start": v(-0.3, 73.67) * mm, "end": v(-0.89, 73.67) * mm});
            skLineSegment(sketch, "E349", {"start": v(-0.89, 73.67) * mm, "end": v(-1.7, 73.48) * mm});
            skLineSegment(sketch, "E350", {"start": v(1.03, 71.33) * mm, "end": v(0.39, 71.57) * mm});
            skLineSegment(sketch, "E351", {"start": v(0.39, 71.57) * mm, "end": v(-0.45, 71.58) * mm});
            skLineSegment(sketch, "E352", {"start": v(-0.45, 71.58) * mm, "end": v(-0.93, 71.26) * mm});
            skLineSegment(sketch, "E353", {"start": v(-0.93, 71.26) * mm, "end": v(-1.15, 70.76) * mm});
            skLineSegment(sketch, "E354", {"start": v(-1.15, 70.76) * mm, "end": v(-1.15, 70.15) * mm});
            skLineSegment(sketch, "E355", {"start": v(-1.15, 70.15) * mm, "end": v(-0.94, 69.72) * mm});
            skLineSegment(sketch, "E356", {"start": v(-0.94, 69.72) * mm, "end": v(-0.65, 69.48) * mm});
            skLineSegment(sketch, "E357", {"start": v(-0.65, 69.48) * mm, "end": v(-0.49, 69.47) * mm});
            skLineSegment(sketch, "E358", {"start": v(-0.49, 69.47) * mm, "end": v(-0.43, 69.4) * mm});
            skLineSegment(sketch, "E359", {"start": v(-0.43, 69.4) * mm, "end": v(-0.46, 69.3) * mm});
            skLineSegment(sketch, "E360", {"start": v(-0.46, 69.3) * mm, "end": v(-0.7, 69.18) * mm});
            skLineSegment(sketch, "E361", {"start": v(-0.7, 69.18) * mm, "end": v(-1.1, 69) * mm});
            skLineSegment(sketch, "E362", {"start": v(-1.1, 69) * mm, "end": v(-1.54, 68.9) * mm});
            skLineSegment(sketch, "E363", {"start": v(-1.54, 68.9) * mm, "end": v(-1.9, 68.82) * mm});
            skLineSegment(sketch, "E364", {"start": v(-1.9, 68.82) * mm, "end": v(-2.22, 68.87) * mm});
            skLineSegment(sketch, "E365", {"start": v(-2.22, 68.87) * mm, "end": v(-3.13, 69.77) * mm});
            skLineSegment(sketch, "E366", {"start": v(-3.13, 69.77) * mm, "end": v(-3.49, 70.47) * mm});
            skLineSegment(sketch, "E367", {"start": v(-3.49, 70.47) * mm, "end": v(-3.62, 71.3) * mm});
            skLineSegment(sketch, "E368", {"start": v(-3.62, 71.3) * mm, "end": v(-3, 72.19) * mm});
            skLineSegment(sketch, "E369", {"start": v(-3, 72.19) * mm, "end": v(-2, 73) * mm});
            skLineSegment(sketch, "E370", {"start": v(-2, 73) * mm, "end": v(-1.33, 73.27) * mm});
            skLineSegment(sketch, "E371", {"start": v(-1.33, 73.27) * mm, "end": v(-0.38, 73.29) * mm});
            skLineSegment(sketch, "E372", {"start": v(-0.38, 73.29) * mm, "end": v(0.34, 73.1) * mm});
            skLineSegment(sketch, "E373", {"start": v(0.34, 73.1) * mm, "end": v(0.78, 72.54) * mm});
            skLineSegment(sketch, "E374", {"start": v(0.78, 72.54) * mm, "end": v(1.18, 72.07) * mm});
            skLineSegment(sketch, "E375", {"start": v(1.18, 72.07) * mm, "end": v(1.17, 71.7) * mm});
            skLineSegment(sketch, "E376", {"start": v(1.17, 71.7) * mm, "end": v(1.03, 71.33) * mm});
            skCircle(sketch, "E377", {"center": v(-0.1, 70.45) * mm, "radius": 0.36 * mm});
            skCircle(sketch, "E378", {"center": v(3.78, 70.38) * mm, "radius": 0.55 * mm});
            skLineSegment(sketch, "E379", {"start": v(3.05, 71.16) * mm, "end": v(2.98, 71.92) * mm});
            skLineSegment(sketch, "E380", {"start": v(2.98, 71.92) * mm, "end": v(3.26, 72.7) * mm});
            skLineSegment(sketch, "E381", {"start": v(3.26, 72.7) * mm, "end": v(3.74, 73.2) * mm});
            skLineSegment(sketch, "E382", {"start": v(3.74, 73.2) * mm, "end": v(4.39, 73.38) * mm});
            skLineSegment(sketch, "E383", {"start": v(4.39, 73.38) * mm, "end": v(5.25, 73.4) * mm});
            skLineSegment(sketch, "E384", {"start": v(5.25, 73.4) * mm, "end": v(5.62, 73.3) * mm});
            skLineSegment(sketch, "E385", {"start": v(5.62, 73.3) * mm, "end": v(6.02, 72.79) * mm});
            skLineSegment(sketch, "E386", {"start": v(6.02, 72.79) * mm, "end": v(6.4, 72.06) * mm});
            skLineSegment(sketch, "E387", {"start": v(6.4, 72.06) * mm, "end": v(6.78, 71.03) * mm});
            skLineSegment(sketch, "E388", {"start": v(6.78, 71.03) * mm, "end": v(6.83, 70.37) * mm});
            skLineSegment(sketch, "E389", {"start": v(6.83, 70.37) * mm, "end": v(6.73, 69.81) * mm});
            skLineSegment(sketch, "E390", {"start": v(6.73, 69.81) * mm, "end": v(6.5, 69.08) * mm});
            skLineSegment(sketch, "E391", {"start": v(6.5, 69.08) * mm, "end": v(6.3, 68.76) * mm});
            skLineSegment(sketch, "E392", {"start": v(6.3, 68.76) * mm, "end": v(5.83, 68.44) * mm});
            skLineSegment(sketch, "E393", {"start": v(5.83, 68.44) * mm, "end": v(5.25, 68.37) * mm});
            skLineSegment(sketch, "E394", {"start": v(5.25, 68.37) * mm, "end": v(4.59, 68.63) * mm});
            skLineSegment(sketch, "E395", {"start": v(4.59, 68.63) * mm, "end": v(4.13, 68.93) * mm});
            skLineSegment(sketch, "E396", {"start": v(4.13, 68.93) * mm, "end": v(3.88, 69.2) * mm});
            skLineSegment(sketch, "E397", {"start": v(3.88, 69.2) * mm, "end": v(4.53, 69.2) * mm});
            skLineSegment(sketch, "E398", {"start": v(4.53, 69.2) * mm, "end": v(4.94, 69.3) * mm});
            skLineSegment(sketch, "E399", {"start": v(4.94, 69.3) * mm, "end": v(5.23, 69.74) * mm});
            skLineSegment(sketch, "E400", {"start": v(5.23, 69.74) * mm, "end": v(5.43, 70.36) * mm});
            skLineSegment(sketch, "E401", {"start": v(5.43, 70.36) * mm, "end": v(5.25, 71) * mm});
            skLineSegment(sketch, "E402", {"start": v(5.25, 71) * mm, "end": v(4.72, 71.35) * mm});
            skLineSegment(sketch, "E403", {"start": v(4.72, 71.35) * mm, "end": v(4.05, 71.35) * mm});
            skLineSegment(sketch, "E404", {"start": v(4.05, 71.35) * mm, "end": v(3.48, 71.27) * mm});
            skLineSegment(sketch, "E405", {"start": v(3.48, 71.27) * mm, "end": v(3.05, 71.16) * mm});
            skLineSegment(sketch, "E406", {"start": v(2.78, 70.78) * mm, "end": v(2.67, 71.22) * mm});
            skLineSegment(sketch, "E407", {"start": v(2.67, 71.22) * mm, "end": v(2.63, 71.76) * mm});
            skLineSegment(sketch, "E408", {"start": v(2.63, 71.76) * mm, "end": v(2.8, 72.46) * mm});
            skLineSegment(sketch, "E409", {"start": v(2.8, 72.46) * mm, "end": v(3.16, 73.04) * mm});
            skLineSegment(sketch, "E410", {"start": v(3.16, 73.04) * mm, "end": v(3.7, 73.49) * mm});
            skLineSegment(sketch, "E411", {"start": v(3.7, 73.49) * mm, "end": v(4.43, 73.68) * mm});
            skLineSegment(sketch, "E412", {"start": v(4.43, 73.68) * mm, "end": v(5.03, 73.72) * mm});
            skLineSegment(sketch, "E413", {"start": v(5.03, 73.72) * mm, "end": v(5.52, 73.68) * mm});
            skLineSegment(sketch, "E414", {"start": v(5.52, 73.68) * mm, "end": v(6.02, 73.45) * mm});
            skLineSegment(sketch, "E415", {"start": v(6.02, 73.45) * mm, "end": v(6.39, 73.1) * mm});
            skLineSegment(sketch, "E416", {"start": v(6.39, 73.1) * mm, "end": v(6.66, 72.56) * mm});
            skLineSegment(sketch, "E417", {"start": v(6.66, 72.56) * mm, "end": v(7.08, 71.8) * mm});
            skLineSegment(sketch, "E418", {"start": v(7.08, 71.8) * mm, "end": v(7.28, 71.14) * mm});
            skLineSegment(sketch, "E419", {"start": v(7.28, 71.14) * mm, "end": v(7.22, 70.6) * mm});
            skLineSegment(sketch, "E420", {"start": v(7.22, 70.6) * mm, "end": v(7.05, 70.01) * mm});
            skLineSegment(sketch, "E421", {"start": v(7.05, 70.01) * mm, "end": v(6.9, 69.34) * mm});
            skLineSegment(sketch, "E422", {"start": v(6.9, 69.34) * mm, "end": v(6.66, 68.73) * mm});
            skLineSegment(sketch, "E423", {"start": v(6.66, 68.73) * mm, "end": v(6.1, 68.3) * mm});
            skLineSegment(sketch, "E424", {"start": v(6.1, 68.3) * mm, "end": v(5.74, 68.1) * mm});
            skLineSegment(sketch, "E425", {"start": v(5.74, 68.1) * mm, "end": v(5.18, 68) * mm});
            skLineSegment(sketch, "E426", {"start": v(5.18, 68) * mm, "end": v(4.63, 68.22) * mm});
            skLineSegment(sketch, "E427", {"start": v(4.63, 68.22) * mm, "end": v(3.95, 68.63) * mm});
            skLineSegment(sketch, "E428", {"start": v(3.95, 68.63) * mm, "end": v(3.42, 69.22) * mm});
            skLineSegment(sketch, "E429", {"start": v(3.42, 69.22) * mm, "end": v(3.14, 69.51) * mm});
            skLineSegment(sketch, "E430", {"start": v(3.14, 69.51) * mm, "end": v(2.73, 69.84) * mm});
            skLineSegment(sketch, "E431", {"start": v(2.73, 69.84) * mm, "end": v(2.66, 70.3) * mm});
            skLineSegment(sketch, "E432", {"start": v(2.66, 70.3) * mm, "end": v(2.78, 70.78) * mm});
            skLineSegment(sketch, "E433", {"start": v(11.17, 70.24) * mm, "end": v(10.84, 70.04) * mm});
            skLineSegment(sketch, "E434", {"start": v(10.84, 70.04) * mm, "end": v(10.65, 69.86) * mm});
            skLineSegment(sketch, "E435", {"start": v(10.65, 69.86) * mm, "end": v(10.8, 69.74) * mm});
            skLineSegment(sketch, "E436", {"start": v(10.8, 69.74) * mm, "end": v(11.24, 69.69) * mm});
            skLineSegment(sketch, "E437", {"start": v(11.24, 69.69) * mm, "end": v(11.82, 69.77) * mm});
            skLineSegment(sketch, "E438", {"start": v(11.82, 69.77) * mm, "end": v(12.11, 69.84) * mm});
            skLineSegment(sketch, "E439", {"start": v(12.11, 69.84) * mm, "end": v(12.04, 70) * mm});
            skLineSegment(sketch, "E440", {"start": v(12.04, 70) * mm, "end": v(11.8, 70.18) * mm});
            skLineSegment(sketch, "E441", {"start": v(11.8, 70.18) * mm, "end": v(11.38, 70.28) * mm});
            skLineSegment(sketch, "E442", {"start": v(11.38, 70.28) * mm, "end": v(11.17, 70.24) * mm});
            skLineSegment(sketch, "E443", {"start": v(-9.45, 64.34) * mm, "end": v(-8.34, 64.34) * mm});
            skSolve(sketch);
        }
        {
            var Q0;
            Q0 = qSketchRegion(id + "F8", true);
            var Q1;
            Q1=makeQuery(id+"F5.opRevolve","SWEPT_FACE",FACE,{"disambiguationData":[OSD([sQuery(id+"F4.wireOp",EDGE,"E8")])]});
            extrude(context, id + "F10", {"entities" : qUnion([Q0]), "operationType" : NewBodyOperationType.ADD, "endBound" : BoundingType.UP_TO_SURFACE, "oppositeDirection" : true, "endBoundEntityFace" : qUnion([Q1]), "depth" : 25 * mm});
        }
        {
            var Q0;
            Q0=makeQuery(id+"F9.imprint","IMPRINT",FACE,{"disambiguationData":[TD([[makeQuery(id+"F9.imprint","IMPRINT",EDGE,{"derivedFrom":sQuery(id+"F9.wireOp",EDGE,"E330")}),1.0]])]});
            var Q1;
            Q1=makeQuery(id+"F9.imprint","IMPRINT",FACE,{"disambiguationData":[TD([[makeQuery(id+"F9.imprint","IMPRINT",EDGE,{"derivedFrom":sQuery(id+"F9.wireOp",EDGE,"E378")}),-1.0]])]});
            var Q2;
            Q2=makeQuery(id+"F9.imprint","IMPRINT",FACE,{"disambiguationData":[TD([[makeQuery(id+"F9.imprint","IMPRINT",EDGE,{"derivedFrom":sQuery(id+"F9.wireOp",EDGE,"E164")}),-1.0]])]});
            var Q3;
            Q3=makeQuery(id+"F9.imprint","IMPRINT",FACE,{"disambiguationData":[TD([[makeQuery(id+"F9.imprint","IMPRINT",EDGE,{"derivedFrom":sQuery(id+"F9.wireOp",EDGE,"E21")}),1.0]])]});
            var Q4;
            Q4=makeQuery(id+"F10.boolean.opBoolean","SPLIT",FACE,{"disambiguationData":[TD([makeQuery(id+"F5.opRevolve","SWEPT_FACE",FACE,{"disambiguationData":[OSD([sQuery(id+"F4.wireOp",EDGE,"E7")])]})])],"derivedFrom":makeQuery(id+"F5.opRevolve","SWEPT_FACE",FACE,{"disambiguationData":[OSD([sQuery(id+"F4.wireOp",EDGE,"E8")])]})});
            extrude(context, id + "F11", {"entities" : qUnion([Q0, Q1, Q2, Q3]), "operationType" : NewBodyOperationType.ADD, "endBound" : BoundingType.UP_TO_SURFACE, "endBoundEntityFace" : qUnion([Q4]), "depth" : 25 * mm});
        }
        {
            var Q0;
            Q0=makeQuery(id+"F4.imprint","IMPRINT",FACE,{"disambiguationData":[TD([[makeQuery(id+"F4.imprint","IMPRINT",EDGE,{"derivedFrom":sQuery(id+"F4.wireOp",EDGE,"E11")}),1.0]])]});
            var Q1;
            Q1=sQuery(id+"F4.wireOp",EDGE,"E4");
            revolve(context, id + "F12", {"operationType" : NewBodyOperationType.REMOVE, "entities" : qUnion([Q0]), "axis" : qUnion([Q1]), "revolveType" : RevolveType.FULL, "oppositeDirection" : true});
        }
    });
